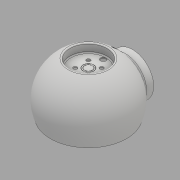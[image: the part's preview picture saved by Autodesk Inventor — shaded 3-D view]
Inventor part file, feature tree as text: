
AUTODESK INVENTOR PART (.ipt)
format: ipt  version: 2020 (Build 240168000, 168)  size: 925,696 bytes
history: native  units: mm
features: sketch x16, extrude x11, other x7, fillet x5, hole x5, revolve x4, plane x4, projected_geometry x3, thicken_offset x2, chamfer x1, reference x1
ambient origin geometry x8: Origin, YZ Plane, XZ Plane, XY Plane, X Axis, Y Axis, Z Axis, Center Point
bodies: Body (feature_tree)
feature tree (59):
  revolve  "Revolution1"  Angle=135.0deg
  revolve  "Revolution2"  [1 undecoded]
  thicken_offset  "Thicken1"
  plane  "Work Plane3"
  extrude  "Back Hole"  Depth=0.4mm
  fillet  "Fillet2"  Radius=67.2mm
  hole  "DC jack"  [1 undecoded]
  hole  "Pot holes"  [1 undecoded]
  extrude  "Button"  Depth=10.0mm
  hole  "Hole8"  [1 undecoded]
  extrude  "Add"  Depth=2.0mm
  extrude  "remove"  Depth=2.0mm
  extrude  "Remove2"  Depth=2.0mm
  fillet  "Fillet7"  Radius=2.0mm
  chamfer  "Chamfer2"  Distance=20.0mm Angle=360.0deg
  fillet  "Fillet8"  [1 undecoded]
  extrude  "Remove3"  Depth=76.0mm
  hole  "PCB holes"  [1 undecoded]
  revolve  "Revolution8"  [1 undecoded]
  thicken_offset  "Thicken2"
  fillet  "Fillet10"  Radius=2.15mm
  plane  "Work Plane9"
  extrude  "Extrusion31"  Depth=2.0mm
  extrude  "Extrusion34"  Depth=28.0mm
  hole  "Hole12"  [1 undecoded]
  extrude  "To better print holes"  Depth=2.7mm
  extrude  "To better print holes2"  Depth=2.7mm
  plane  "Work Plane11"
  revolve  "Revolution10"  Angle=360.0deg
  fillet  "Fillet11"  Radius=2.0mm
  plane  "Work Plane12"
  other  "LightSensor hole"
  extrude  "Extrusion39"  Depth=2.7mm
  sketch  "Sketch2"  dims[d0=90.0deg d13=135.0deg]
  other  "Shield"
  sketch  "Sketch6"  dims[d14=3.0mm d15=1.5mm]
  sketch  "Sketch29"  dims[d26=90.0deg d27=0.4mm d28=0.2mm d38=67.2mm]
  projected_geometry  "Projected Loop9"
  sketch  "Sketch46"  dims[d60=26.0mm d61=0.0mm d72=2.0mm]
  sketch  "Sketch47"  dims[d89=15.0mm d95=45.0deg]
  sketch  "Sketch48"  dims[d96=40.0mm d98=360.0deg d100=10.0mm]
  sketch  "Sketch49"  dims[d101=10.0mm d170=66.473715mm]
  other  "Stand"
  sketch  "Sketch52"  dims[d191=10.0mm d192=10.0mm d193=3.0mm d194=6.0mm d195=4.0mm d196=2.0mm d197=90.0deg d198=8.0mm d199=20.594885mm d204=67.05mm]
  sketch  "Sketch54"  dims[d218=2.0mm d219=2.0mm]
  sketch  "Sketch55"  dims[d222=0.5mm d229=7.5mm d231=2.0mm d232=20.0mm d234=360.0deg d236=0.0mm d237=0.0mm]
  other  "Diffuser"
  sketch  "Sketch56"  dims[d247=26.0mm d249=76.0mm]
  sketch  "Sketch57"  dims[d251=2.0mm d255=5.0mm]
  sketch  "Sketch58"  dims[d258=13.4mm d259=0.0mm d260=4.3mm d261=0.0mm d262=2.15mm]
  sketch  "Sketch59"  dims[d265=0.5mm d266=2.0mm d267=45.0deg d272=1.0mm]
  sketch  "Sketch63"  dims[d295=3.0mm d299=28.0mm]
  projected_geometry  "Projected Loop13"
  reference  "Reference7"
  projected_geometry  "Projected Loop14"
  sketch  "Sketch66"  dims[d300=10.4mm d301=6.0mm d302=4.0mm d303=2.0mm d304=90.0deg d305=8.0mm d306=20.594885mm d307=15.0mm d309=7.2mm d310=6.0mm d311=4.0mm d312=2.0mm d313=90.0deg d314=8.0mm d315=20.594885mm d318=85.0mm d319=30.0mm d321=360.0deg d323=5.0mm d324=6.0mm d325=19.05mm d326=4.775mm d327=90.0deg d328=10.0mm d329=0.0mm d334=2.0mm d336=6.0mm d337=40.0mm d338=90.0deg d339=2.0mm d355=-0.48mm d357=60.0mm d358=10.35mm d360=360.0deg d363=5.000016mm d364=4.4mm d365=0.0mm d366=0.5mm d367=0.2mm d368=1.0mm d370=35.0mm d371=77.5mm d377=0.16mm d378=0.0mm d380=2.0mm d381=0.0mm d382=0.4mm d395=7.9mm d396=3.2mm d397=0.5mm d399=3.0mm d400=7.4mm d401=0.0mm d402=5.0mm d403=1.0mm d407=3.0mm d408=1.8mm d409=7.9mm d410=1.95mm d411=7.4mm d412=0.0mm d413=4.2mm d414=8.0mm d415=7.2mm d416=4.2mm d417=90.0deg d418=8.0mm d419=20.594885mm d420=0.16mm d421=0.0mm d428=-2.268928mm d430=5.726141mm d431=5.226141mm d432=0.959931mm d433=0.8mm d434=2.7mm d435=2.7mm d436=2.5mm d437=0.762mm d438=2.54mm d442=0.0mm d443=0.5mm d444=30.0mm d445=30.0mm d446=30.0mm d447=0.0mm d142=1.0mm d143=1.0mm d238=0.5mm d239=0.872665mm d240=0.5mm d241=0.872665mm d248=0.872665mm d250=0.872665mm d252=0.872665mm d293=0.5mm d294=0.872665mm d296=0.872665mm d383=0.872665mm]
  parser-record x1  (decoder bookkeeping rows leaked as tree rows — omitted from the tree; the rows remain in map.json)
  other  "Assembly.iam"
  other  "PCB:1"
note: 8 required parameter values undecoded (feature->parameter linkage not recoverable at this tier; creation-order binding heuristic only, values carry confidence <= 0.55)
note: 1 file-system path scrubbed to <path> (originals preserved in map.json)